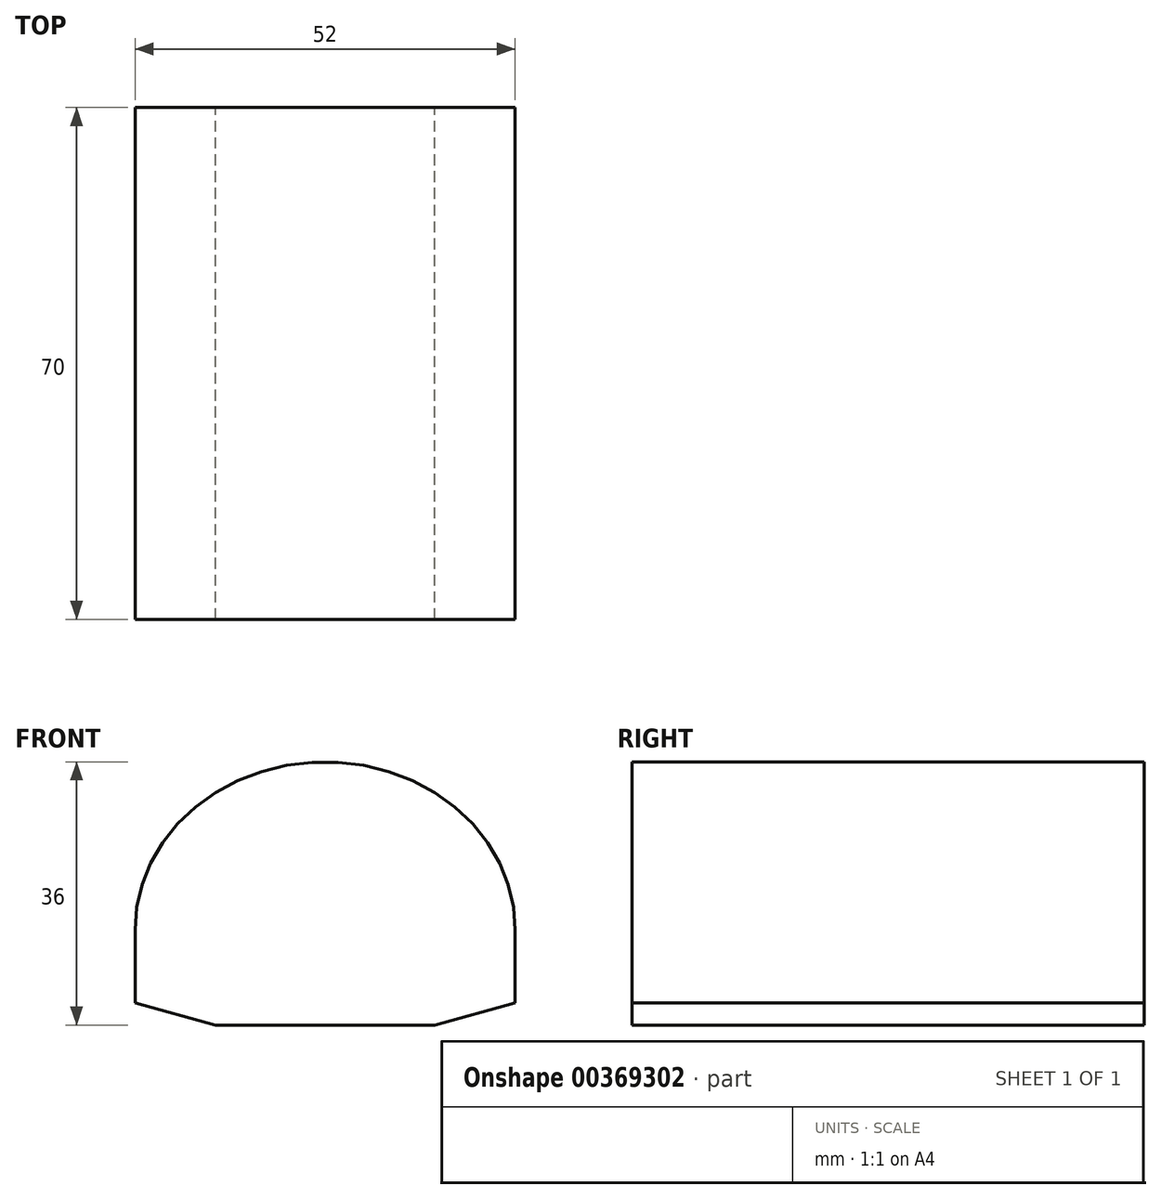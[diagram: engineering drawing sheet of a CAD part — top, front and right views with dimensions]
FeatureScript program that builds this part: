
annotation { "Feature Type Name" : "Feature", "Feature Type Description" : "" }
export const myFeature = defineFeature(function(context is Context, id is Id, definition is map)
    precondition{}
    {
        {
            var Q0;
            Q0=qCreatedBy(makeId("Front.planeOp"),FACE);
            var sketch = newSketch(context, id + "F0", { "sketchPlane" : qUnion([Q0])});
            skEllipticalArc(sketch, "E0", {});
            skLineSegment(sketch, "E1", {"start": v(-26, 0) * mm, "end": v(26, 0) * mm, "construction": true});
            skLineSegment(sketch, "E2", {"start": v(0, 0) * mm, "end": v(0, 23) * mm, "construction": true});
            skLineSegment(sketch, "E3", {"start": v(-15, -13) * mm, "end": v(15, -13) * mm});
            skLineSegment(sketch, "E4", {"start": v(-15, -13) * mm, "end": v(-26, -10) * mm});
            skLineSegment(sketch, "E5", {"start": v(15, -13) * mm, "end": v(26, -10) * mm});
            skLineSegment(sketch, "E6", {"start": v(-26, 0) * mm, "end": v(-26, -10) * mm});
            skLineSegment(sketch, "E7", {"start": v(26, -10) * mm, "end": v(26, 0) * mm});
            const initialGuessF0  = {"E0": [0, 0, 1, 0, 0.026, 0.023, 0, 3.141592653589793]};
            skSetInitialGuess(sketch, initialGuessF0);
            skSolve(sketch);
        }
        {
            var Q0;
            Q0 = qSketchRegion(id + "F0", true);
            extrude(context, id + "F1", {"entities" : qUnion([Q0]), "depth" : 70 * mm});
        }
    });
